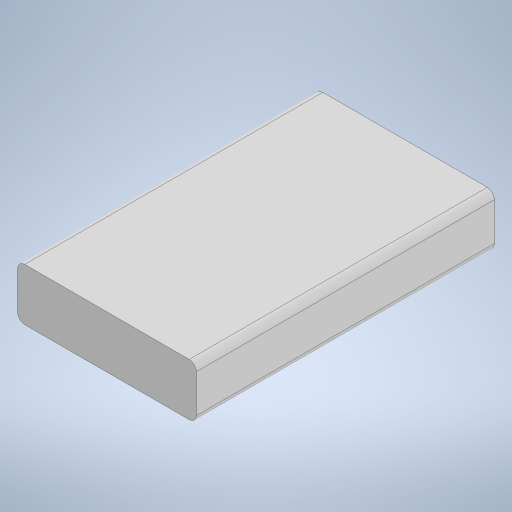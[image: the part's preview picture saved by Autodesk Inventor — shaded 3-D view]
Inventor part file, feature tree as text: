
AUTODESK INVENTOR PART (.ipt)
format: ipt  version: 2023 (Build 270158000, 158)  size: 204,800 bytes
history: native  units: mm
features: fillet x2, other x1, extrude x1, sketch x1
ambient origin geometry x8: Origin, YZ Plane, XZ Plane, XY Plane, X Axis, Y Axis, Z Axis, Center Point
bodies: Body1 (feature_tree)
feature tree (5):
  other  "Bryła1"
  extrude  "Wyciągnięcie proste1"  Depth=15.0mm
  fillet  "Zaokrąglenie1"  Radius=25.0mm
  fillet  "Zaokrąglenie2"  Radius=4.38mm
  sketch  "Szkic1"
